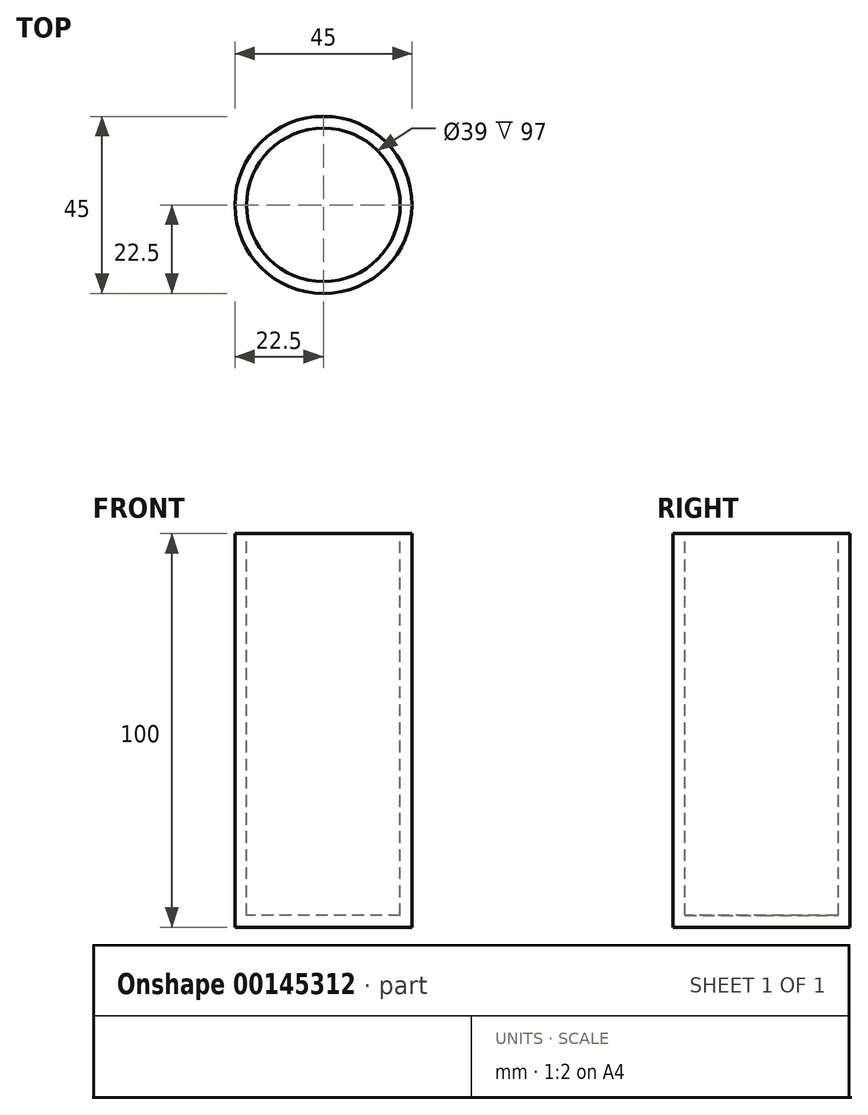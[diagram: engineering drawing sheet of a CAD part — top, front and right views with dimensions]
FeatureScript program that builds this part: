
annotation { "Feature Type Name" : "Feature", "Feature Type Description" : "" }
export const myFeature = defineFeature(function(context is Context, id is Id, definition is map)
    precondition{}
    {
        {
            var Q0;
            Q0=qCreatedBy(makeId("Front.planeOp"),FACE);
            var sketch = newSketch(context, id + "F0", { "sketchPlane" : qUnion([Q0])});
            skLineSegment(sketch, "E0.bottom", {"start": v(0, 0) * mm, "end": v(-22.5, 0) * mm});
            skLineSegment(sketch, "E0.top", {"start": v(0, 100) * mm, "end": v(-22.5, 100) * mm});
            skLineSegment(sketch, "E0.left", {"start": v(0, 0) * mm, "end": v(0, 100) * mm});
            skLineSegment(sketch, "E0.right", {"start": v(-22.5, 0) * mm, "end": v(-22.5, 100) * mm});
            skLineSegment(sketch, "E1.bottom", {"start": v(0, 100) * mm, "end": v(-19.5, 100) * mm});
            skLineSegment(sketch, "E1.top", {"start": v(0, 3) * mm, "end": v(-19.5, 3) * mm});
            skLineSegment(sketch, "E1.left", {"start": v(0, 100) * mm, "end": v(0, 3) * mm});
            skLineSegment(sketch, "E1.right", {"start": v(-19.5, 100) * mm, "end": v(-19.5, 3) * mm});
            skSolve(sketch);
        }
        {
            var Q0;
            Q0=makeQuery(id+"F0.imprint","IMPRINT",FACE,{"disambiguationData":[TD([[makeQuery(id+"F0.imprint","IMPRINT",EDGE,{"derivedFrom":sQuery(id+"F0.wireOp",EDGE,"E0.bottom")}),-1.0]])]});
            var Q1;
            Q1=sQuery(id+"F0.wireOp",EDGE,"E1.left");
            revolve(context, id + "F1", {"entities" : qUnion([Q0]), "axis" : qUnion([Q1]), "revolveType" : RevolveType.FULL});
        }
    });
